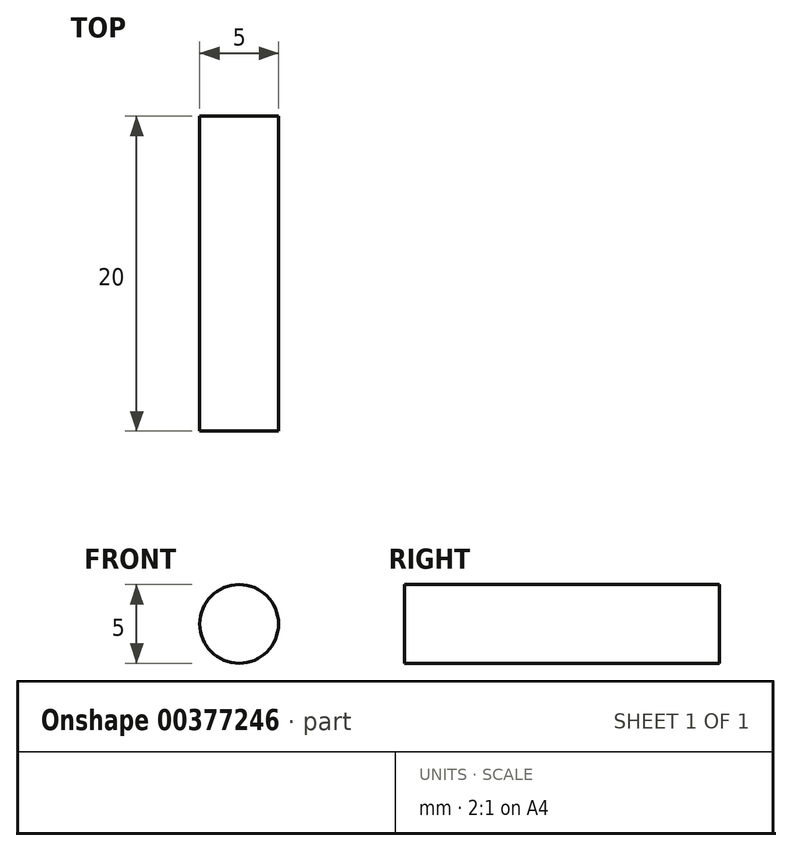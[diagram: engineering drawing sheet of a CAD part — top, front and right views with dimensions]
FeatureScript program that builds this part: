
annotation { "Feature Type Name" : "Feature", "Feature Type Description" : "" }
export const myFeature = defineFeature(function(context is Context, id is Id, definition is map)
    precondition{}
    {
        {
            var Q0;
            Q0=qCreatedBy(makeId("Front.planeOp"),FACE);
            var sketch = newSketch(context, id + "F0", { "sketchPlane" : qUnion([Q0])});
            skCircle(sketch, "E0", {"center": v(0, 0) * mm, "radius": 2.5 * mm});
            skSolve(sketch);
        }
        {
            var Q0;
            Q0=makeQuery(id+"F0.imprint","IMPRINT",FACE,{"disambiguationData":[TD([[makeQuery(id+"F0.imprint","IMPRINT",EDGE,{"derivedFrom":sQuery(id+"F0.wireOp",EDGE,"E0")}),1.0]])]});
            extrude(context, id + "F1", {"entities" : qUnion([Q0]), "depth" : 20 * mm});
        }
    });
